# Revit family: RRHFB
name_source: partatom
category: Generic Models
revit_build: Autodesk Revit 2018 (Build: 20190510_1515(x64)
units: mm (PartAtom-declared; Revit-internal decimal feet)

## family parameters
Always vertical = No
Can host rebar = No
Cut with Voids When Loaded = No
Part Type = Normal
Room Calculation Point = No
Round Connector Dimension = Use Diameter
Shared = Yes
Work Plane-Based = Yes

## types (7) — shared parameters
Bolt Material = <By Category>
Default Elevation = 48 "

## per-type parameters (varying)
| type | Bolt Radius | Description | Head Height | Head Point Width | Head Width | Length | Nominal Size | Washer Radius |
| RRHFB38162 | 0.188 " | Flange Bolt Hex Head Stainless 3/8-16 X 2 Inch long | 0.25 " | 0.65 " | 0.563 " | 2 " | 0.375 " | 0.375 " |
| RRHFB38161 | 0.188 " | Flange Bolt Hex Head Stainless 3/8-16 X 1 Inch long | 0.25 " | 0.65 " | 0.563 " | 1 " | 0.375 " | 0.375 " |
| RRHFB38163 | 0.188 " | Flange Bolt Hex Head Stainless 3/8-16 X 3 Inch long | 0.25 " | 0.65 " | 0.563 " | 3 " | 0.375 " | 0.375 " |
| RRHFB14201/2 | 0.125 " | Flange Bolt Hex Head Stainless 1/4-20 X 1/2 Inch long | 0.172 " | 0.506 " | 0.438 " | 0.5 " | 0.25 " | 0.303 " |
| RRHFB14202 | 0.125 " | Flange Bolt Hex Head Stainless 1/4-20 X 2 Inch long | 0.172 " | 0.506 " | 0.438 " | 2 " | 0.25 " | 0.303 " |
| RRHFB14203 | 0.125 " | Flange Bolt Hex Head Stainless 1/4-20 X 3 Inch long | 0.172 " | 0.506 " | 0.438 " | 3 " | 0.25 " | 0.303 " |
| RRHFB38163/4 | 0.188 " | Flange Bolt Hex Head Stainless 3/8-16 X 3/4 Inch long | 0.25 " | 0.65 " | 0.563 " | 0.75 " | 0.375 " | 0.375 " |

note: column(s) folded — value = type name in every type: Catalog Number

## geometry (parser evidence)
native form markers: Sweep x3
no freeform markers — native parametric forms only
